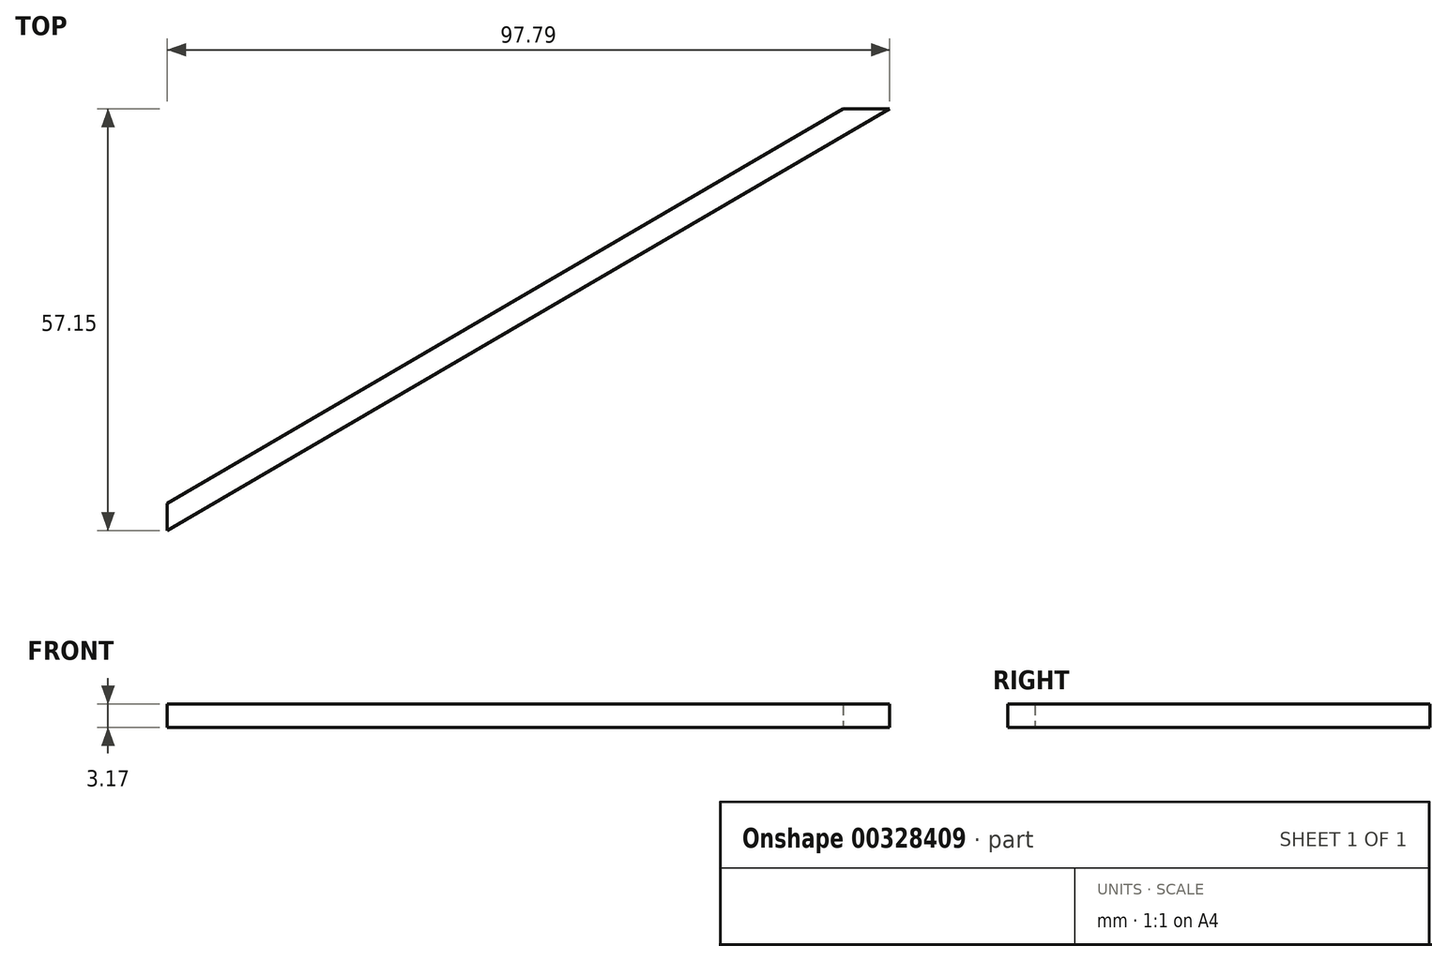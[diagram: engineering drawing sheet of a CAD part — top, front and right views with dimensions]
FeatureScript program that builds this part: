
annotation { "Feature Type Name" : "Feature", "Feature Type Description" : "" }
export const myFeature = defineFeature(function(context is Context, id is Id, definition is map)
    precondition{}
    {
        {
            var Q0;
            Q0=qCreatedBy(makeId("Top.planeOp"),FACE);
            var sketch = newSketch(context, id + "F0", { "sketchPlane" : qUnion([Q0])});
            skLineSegment(sketch, "E0", {"start": v(0, 0) * mm, "end": v(0, 57.15) * mm});
            skLineSegment(sketch, "E1", {"start": v(0, 57.15) * mm, "end": v(97.8, 57.15) * mm});
            skLineSegment(sketch, "E2", {"start": v(0, 0) * mm, "end": v(123.2, 0) * mm});
            skLineSegment(sketch, "E3", {"start": v(123.2, 0) * mm, "end": v(123.2, 57.15) * mm});
            skLineSegment(sketch, "E4", {"start": v(0, 0) * mm, "end": v(97.8, 57.15) * mm});
            skLineSegment(sketch, "E5", {"start": v(0, 3.68) * mm, "end": v(91.5, 57.15) * mm});
            skSolve(sketch);
        }
        {
            var Q0;
            {var subQ0=sQuery(id+"F0.wireOp",EDGE,"E4");Q0=makeQuery(id+"F0.imprint","IMPRINT",FACE,{"disambiguationData":[TD([[makeQuery(id+"F0.imprint","IMPRINT",EDGE,{"derivedFrom":subQ0}),1.0]])]});}
            extrude(context, id + "F1", {"entities" : qUnion([Q0]), "depth" : 3.17 * mm});
        }
    });
